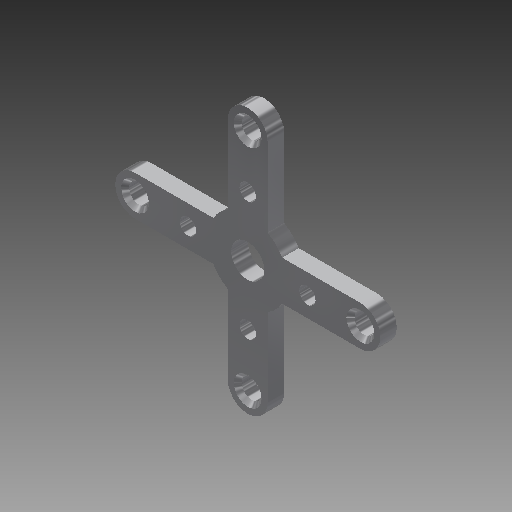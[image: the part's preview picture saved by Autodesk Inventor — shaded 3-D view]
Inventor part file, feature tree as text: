
AUTODESK INVENTOR PART (.ipt)
format: ipt  version: 2019 (Build 230136000, 136)  size: 153,600 bytes
history: native  units: mm
features: extrude x2, sketch x2, pattern_circular x1, chamfer x1
ambient origin geometry x8: Origin, YZ Plane, XZ Plane, XY Plane, X Axis, Y Axis, Z Axis, Center Point
bodies: Solid1 (feature_tree)
feature tree (6):
  extrude  "Extrusion1"  Depth=12.0mm
  extrude  "Extrusion2"  Depth=3.0mm
  pattern_circular  "Circular Pattern1"  [2 undecoded]
  chamfer  "Chamfer1"  Distance=9.0mm
  sketch  "Sketch2"  dims[d12=5.0mm d13=12.0mm]
  sketch  "Sketch3"  dims[d14=2.5mm d15=0.0mm d16=3.0mm d17=2.5mm d18=9.0mm d19=17.0mm d20=3.0mm d21=3.0mm d22=2.5mm d23=0.0mm d24=40.0mm d25=360.0deg d27=0.6mm d28=2.0mm d29=45.0deg]
note: 2 required parameter values undecoded (feature->parameter linkage not recoverable at this tier; creation-order binding heuristic only, values carry confidence <= 0.55)
